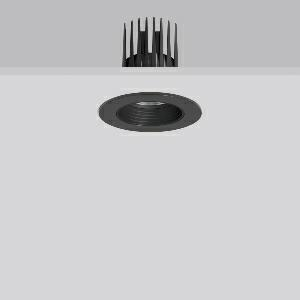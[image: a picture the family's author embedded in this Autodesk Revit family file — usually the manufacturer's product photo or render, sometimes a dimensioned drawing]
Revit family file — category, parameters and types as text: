
# Revit family: heledon_mini_e_901752_003_76_baf9
name_source: partatom
category: Lighting Fixtures
units: mm (PartAtom-declared; Revit-internal decimal feet)

## family parameters
Cut with Voids When Loaded = No
Host = Face
Light Source = No
Part Type = Normal
Room Calculation Point = No
Round Connector Dimension = Use Diameter
Shared = No

## types (1)
- HELEDON mini E (1 x LED Modul 930, 3000 lm, 3000)
    Apparent Load = 29 VA
    Approval mark = CE
    CIE Flux Codes = 96 100 100 100 100
    Color Rendering = 90
    Color Temperature = 3000
    Default Elevation = 1800 mm
    Description = Series: HELEDON mini
Round recessed downlight. Housing: die-cast aluminium, powder-coated. Black plastic ring and recessed LED to prevent glare from the side. Optical assembly with lens made of plastic (polycarbonate) for the best homogeneous light distribution - can be changed without tools. Best colour rendering index Ra>90. Suitable for Recessed ceiling mounting. Installation without tools thanks to spring fastening system. Including separate LED converter with connecting cable 600 mm.High quality converter without flickering and stroboscopic effect. Through-wiring box (5 pole) available as accessory. The following accessories can be mounted without use of tools: interchangeable lenses, decorative glasses, honeycomb louvre, clear and frosted diffusers, white interchangeable plastic ring. 
Colour: deep black, matt (RAL 9005)
Diameter: 124 mm
Height: 3 mm
Cut-out diameter: 114 mm
Recess height: 170 mm
Luminaire: recess height: 120 mm
Lamp: LED
Socket: without socket
Colour temperature: 3000K
Colour rendering index (CRI): 92
System power: 29 W
Rated luminous flux: 3000 lm
Luminous efficiency: 103 lm/W
Control gear: Converter, dimmable, DALI
Protection class: II
Type of protection: IP 20
    Height = 0 mm  [stored 0 ft]
    Lamp = 1 x LED Modul 930
    Lamp Light Flux = 3000 lm
    Lamp count = 1
    Length = 124 mm  [stored 0.406824 ft]
    Lifetime = 50000 h
    Luminous efficacy = 103 lm/W
    Manufacturer = RZB
    ModVariant = No
    Model = 901752.003.76
    Mounting Place = Ceiling
    Mounting Type = Recessed
    Number of Poles = 1
    OnlyDefault = Yes
    Power Factor = 1
    Product Name = HELEDON mini E
    Product group = Recessed downlights
    ProductGroupID = 402
    Protection Class = Protection class II
    Protection Degree = IP 20
    RLX_Detail_Level = 1
    RLX_Emergency_Light_Flux = 0 lm
    RLX_Emergency_Type = 0
    RLX_Emergency_Type_DB = No
    RlxData = <blob elided: 124201 chars, md5=d511afd0>
    Socket = socket
    Standby Power = 0 W
    System Light Flux = 3000 lm
    System Power = 29 W
    Type Comments = Product without accessories
    Type Image = 901656.003.jpg
    URL = http://relux.com
    VarID = ---
    Voltage = 230 V
    Voltage Range = 220-240 V
    Weight = 0.00 kg
    Width = 0 mm  [stored 0 ft]

note: [stored X ft] marks values corroborated as IEEE doubles in the binary element streams (Revit-internal decimal feet)

## geometry (parser evidence)
native form markers: Blend x4, Sweep x11
no freeform markers — native parametric forms only
